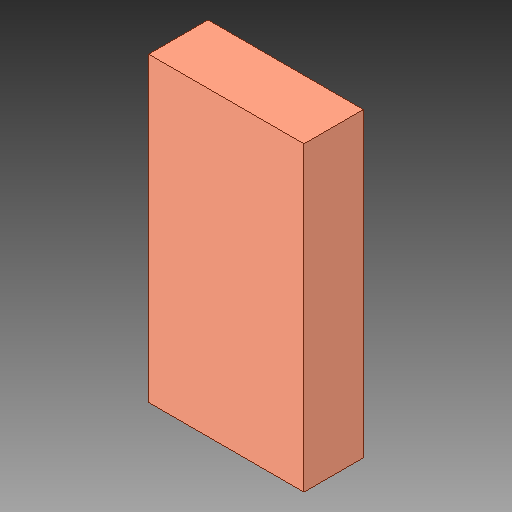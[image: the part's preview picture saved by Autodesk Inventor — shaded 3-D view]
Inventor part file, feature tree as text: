
AUTODESK INVENTOR PART (.ipt)
format: ipt  version: 2018 (Build 220112000, 112)  size: 79,872 bytes
history: native  units: in
note: dims shown in document units (in); Inventor stores cm internally (conversion verified against a paired STEP export)
features: other x1, extrude x1
ambient origin geometry x8: Origin, YZ Plane, XZ Plane, XY Plane, X Axis, Y Axis, Z Axis, Center Point
bodies: Solid1 (feature_tree)
feature tree (2):
  other  "JP1M, _5V_59"
  extrude  "Extrusion1"  Depth=0.0394in TaperAngle=0.0deg
